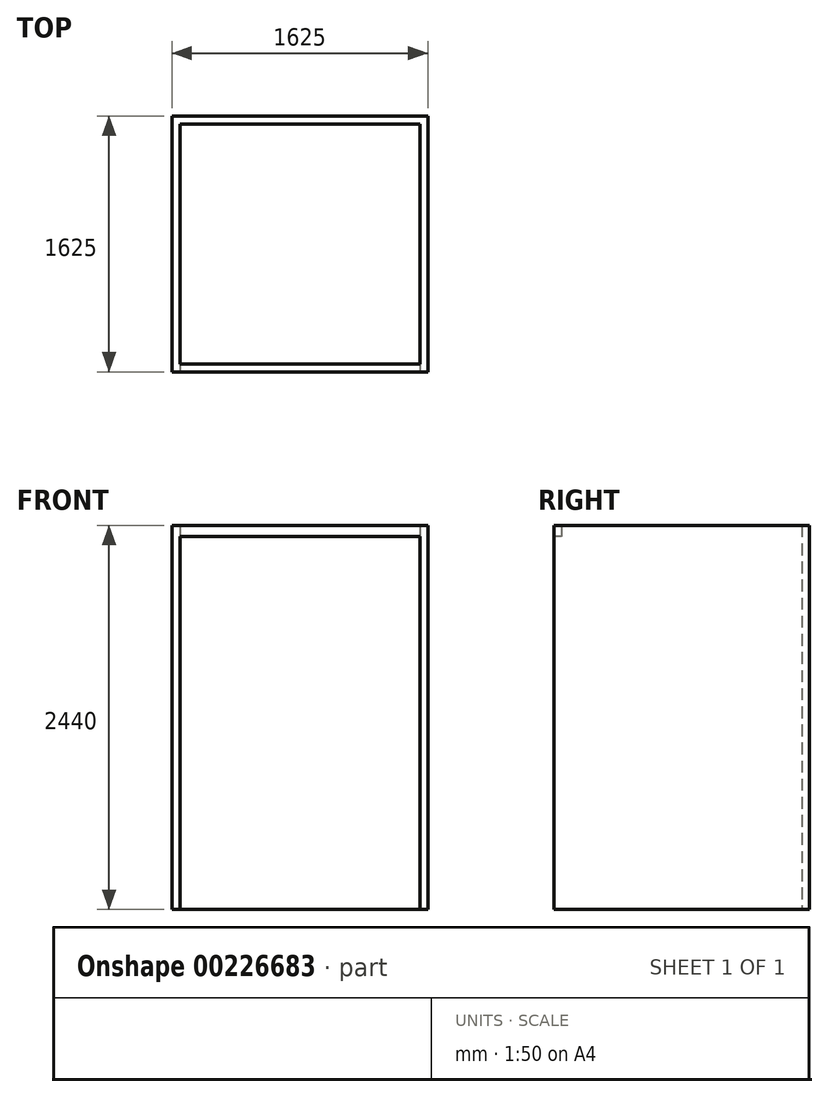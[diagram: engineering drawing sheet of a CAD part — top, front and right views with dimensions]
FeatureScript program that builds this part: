
annotation { "Feature Type Name" : "Feature", "Feature Type Description" : "" }
export const myFeature = defineFeature(function(context is Context, id is Id, definition is map)
    precondition{}
    {
        {
            var Q0;
            Q0=qCreatedBy(makeId("Top.planeOp"),FACE);
            var sketch = newSketch(context, id + "F0", { "sketchPlane" : qUnion([Q0])});
            skLineSegment(sketch, "E0.bottom", {"start": v(762.5, -762.5) * mm, "end": v(-762.5, -762.5) * mm});
            skLineSegment(sketch, "E0.top", {"start": v(762.5, 762.5) * mm, "end": v(-762.5, 762.5) * mm});
            skLineSegment(sketch, "E0.left", {"start": v(762.5, -762.5) * mm, "end": v(762.5, 762.5) * mm});
            skLineSegment(sketch, "E0.right", {"start": v(-762.5, -762.5) * mm, "end": v(-762.5, 762.5) * mm});
            skPoint(sketch, "E0.middle", {"position": v(0, 0) * mm});
            skLineSegment(sketch, "E1.bottom", {"start": v(812.5, -812.5) * mm, "end": v(-812.5, -812.5) * mm});
            skLineSegment(sketch, "E1.top", {"start": v(812.5, 812.5) * mm, "end": v(-812.5, 812.5) * mm});
            skLineSegment(sketch, "E1.left", {"start": v(812.5, -812.5) * mm, "end": v(812.5, 812.5) * mm});
            skLineSegment(sketch, "E1.right", {"start": v(-812.5, -812.5) * mm, "end": v(-812.5, 812.5) * mm});
            skSolve(sketch);
        }
        {
            var Q0;
            Q0=makeQuery(id+"F0.imprint","IMPRINT",FACE,{"disambiguationData":[TD([[makeQuery(id+"F0.imprint","IMPRINT",EDGE,{"derivedFrom":sQuery(id+"F0.wireOp",EDGE,"E0.bottom")}),1.0]])]});
            extrude(context, id + "F1", {"entities" : qUnion([Q0]), "depth" : 2440 * mm});
        }
        {
            var Q0;
            Q0=makeQuery(id+"F1.opExtrude","SWEPT_FACE",FACE,{"disambiguationData":[OSD([sQuery(id+"F0.wireOp",EDGE,"E1.bottom")])]});
            var sketch = newSketch(context, id + "F2", { "sketchPlane" : qUnion([Q0])});
            skLineSegment(sketch, "E2", {"start": v(-762.5, 0) * mm, "end": v(-762.5, 2370) * mm});
            skLineSegment(sketch, "E3", {"start": v(-762.5, 2370) * mm, "end": v(762.5, 2370) * mm});
            skLineSegment(sketch, "E4", {"start": v(762.5, 2370) * mm, "end": v(762.5, 0) * mm});
            skSolve(sketch);
        }
        {
            var Q0;
            {var subQ0=sQuery(id+"F2.wireOp",EDGE,"E2");Q0=makeQuery(id+"F2.imprint","IMPRINT",FACE,{"disambiguationData":[TD([[makeQuery(id+"F2.imprint","IMPRINT",EDGE,{"derivedFrom":subQ0}),-1.0]])]});}
            extrude(context, id + "F3", {"entities" : qUnion([Q0]), "operationType" : NewBodyOperationType.REMOVE, "oppositeDirection" : true, "depth" : 164 * mm});
        }
    });
